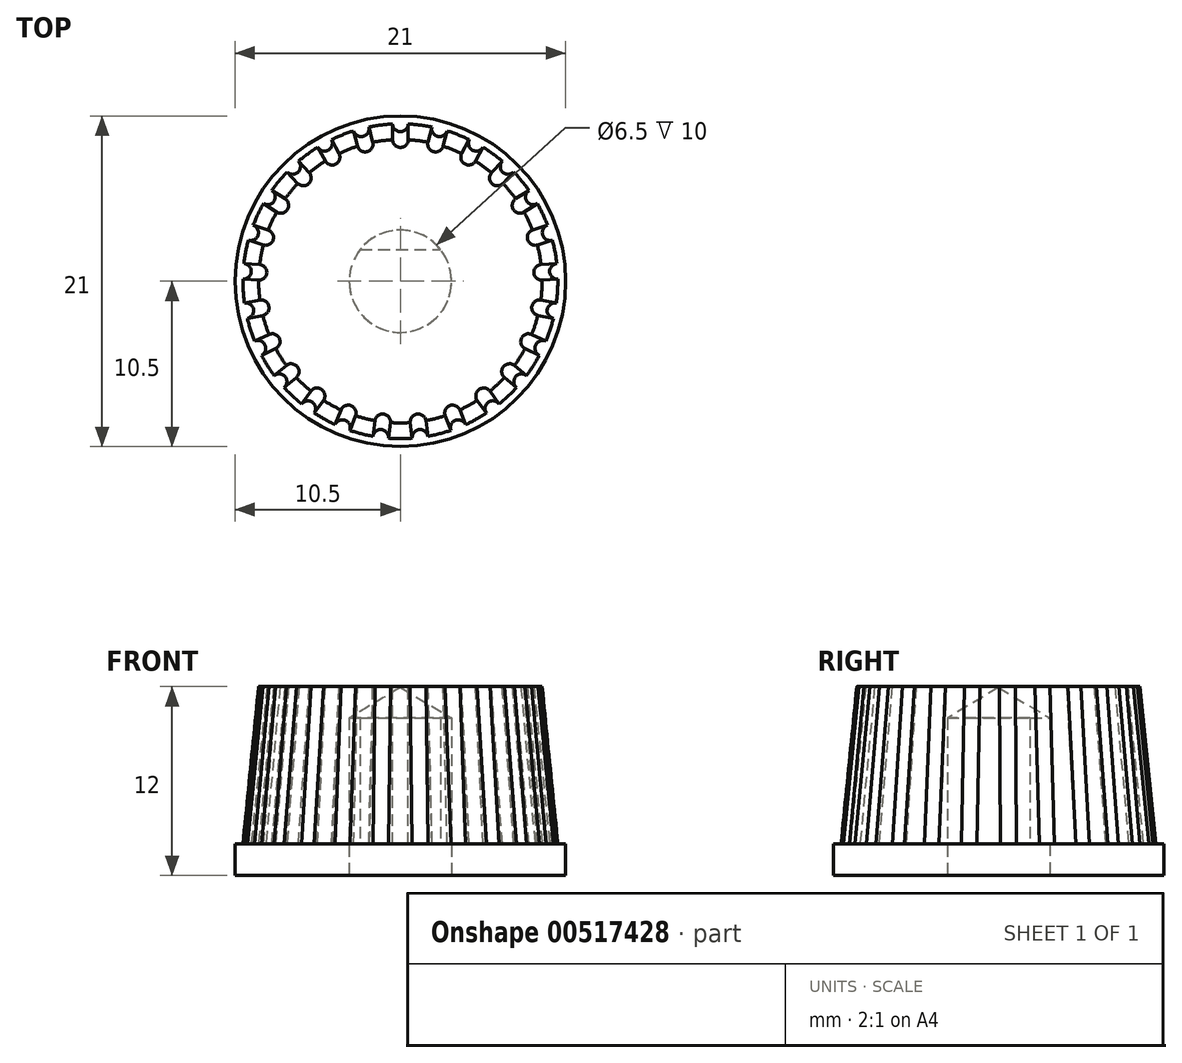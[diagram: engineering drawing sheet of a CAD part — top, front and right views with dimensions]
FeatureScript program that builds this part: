
annotation { "Feature Type Name" : "Feature", "Feature Type Description" : "" }
export const myFeature = defineFeature(function(context is Context, id is Id, definition is map)
    precondition{}
    {
        {
            var Q0;
            Q0=qCreatedBy(makeId("Top.planeOp"),FACE);
            var sketch = newSketch(context, id + "F0", { "sketchPlane" : qUnion([Q0])});
            skCircle(sketch, "E0", {"center": v(0, 0) * mm, "radius": 10 * mm});
            skArc(sketch, "E1", {"start": v(-0.5, 9.99) * mm, "mid": v(0, 9.5) * mm, "end": v(0.5, 9.99) * mm});
            skArc(sketch, "E2.1.0", {"start": v(-2.97, 9.55) * mm, "mid": v(-2.36, 9.2) * mm, "end": v(-2, 9.8) * mm});
            skArc(sketch, "E2.2.0", {"start": v(-5.25, 8.51) * mm, "mid": v(-4.58, 8.32) * mm, "end": v(-4.37, 9) * mm});
            skArc(sketch, "E2.3.0", {"start": v(-7.2, 6.94) * mm, "mid": v(-6.5, 6.93) * mm, "end": v(-6.47, 7.62) * mm});
            skArc(sketch, "E2.4.0", {"start": v(-8.7, 4.93) * mm, "mid": v(-8.02, 5.1) * mm, "end": v(-8.16, 5.77) * mm});
            skArc(sketch, "E2.5.0", {"start": v(-9.65, 2.61) * mm, "mid": v(-9.04, 2.94) * mm, "end": v(-9.34, 3.56) * mm});
            skArc(sketch, "E2.6.0", {"start": v(-10, 0.13) * mm, "mid": v(-9.48, 0.6) * mm, "end": v(-9.94, 1.13) * mm});
            skArc(sketch, "E2.7.0", {"start": v(-9.72, -2.36) * mm, "mid": v(-9.33, -1.78) * mm, "end": v(-9.9, -1.38) * mm});
            skArc(sketch, "E2.8.0", {"start": v(-8.82, -4.7) * mm, "mid": v(-8.6, -4.04) * mm, "end": v(-9.25, -3.8) * mm});
            skArc(sketch, "E2.9.0", {"start": v(-7.38, -6.75) * mm, "mid": v(-7.32, -6.06) * mm, "end": v(-8.01, -5.98) * mm});
            skArc(sketch, "E2.10.0", {"start": v(-5.47, -8.37) * mm, "mid": v(-5.58, -7.69) * mm, "end": v(-6.27, -7.79) * mm});
            skArc(sketch, "E2.11.0", {"start": v(-3.21, -9.47) * mm, "mid": v(-3.5, -8.83) * mm, "end": v(-4.14, -9.1) * mm});
            skArc(sketch, "E2.12.0", {"start": v(-0.76, -9.97) * mm, "mid": v(-1.2, -9.43) * mm, "end": v(-1.75, -9.85) * mm});
            skArc(sketch, "E2.13.0", {"start": v(1.75, -9.85) * mm, "mid": v(1.2, -9.43) * mm, "end": v(0.76, -9.97) * mm});
            skArc(sketch, "E2.14.0", {"start": v(4.14, -9.1) * mm, "mid": v(3.5, -8.83) * mm, "end": v(3.21, -9.47) * mm});
            skArc(sketch, "E2.15.0", {"start": v(6.27, -7.79) * mm, "mid": v(5.58, -7.69) * mm, "end": v(5.47, -8.37) * mm});
            skArc(sketch, "E2.16.0", {"start": v(8.01, -5.98) * mm, "mid": v(7.32, -6.06) * mm, "end": v(7.38, -6.75) * mm});
            skArc(sketch, "E2.17.0", {"start": v(9.25, -3.8) * mm, "mid": v(8.6, -4.04) * mm, "end": v(8.82, -4.7) * mm});
            skArc(sketch, "E2.18.0", {"start": v(9.9, -1.38) * mm, "mid": v(9.33, -1.78) * mm, "end": v(9.72, -2.36) * mm});
            skArc(sketch, "E2.19.0", {"start": v(9.94, 1.13) * mm, "mid": v(9.48, 0.6) * mm, "end": v(10, 0.13) * mm});
            skArc(sketch, "E2.20.0", {"start": v(9.34, 3.56) * mm, "mid": v(9.04, 2.94) * mm, "end": v(9.65, 2.61) * mm});
            skArc(sketch, "E2.21.0", {"start": v(8.16, 5.77) * mm, "mid": v(8.02, 5.1) * mm, "end": v(8.7, 4.93) * mm});
            skArc(sketch, "E2.22.0", {"start": v(6.47, 7.62) * mm, "mid": v(6.5, 6.93) * mm, "end": v(7.2, 6.94) * mm});
            skArc(sketch, "E2.23.0", {"start": v(4.37, 9) * mm, "mid": v(4.58, 8.32) * mm, "end": v(5.25, 8.51) * mm});
            skArc(sketch, "E2.24.0", {"start": v(2, 9.8) * mm, "mid": v(2.36, 9.2) * mm, "end": v(2.97, 9.55) * mm});
            skSolve(sketch);
        }
        {
            var Q0;
            Q0=qCreatedBy(makeId("Top.planeOp"),FACE);
            cPlane(context, id + "F1", {"entities" : qUnion([Q0]), "cplaneType" : CPlaneType.OFFSET, "offset" : 10 * mm, "width" : 150 * mm, "height" : 150 * mm});
        }
        {
            var Q0;
            Q0=qCreatedBy(id+"F1.planeOp",FACE);
            var sketch = newSketch(context, id + "F2", { "sketchPlane" : qUnion([Q0])});
            skCircle(sketch, "E3", {"center": v(0, 0) * mm, "radius": 9 * mm});
            skArc(sketch, "E4", {"start": v(-0.5, 8.99) * mm, "mid": v(0, 8.5) * mm, "end": v(0.5, 8.99) * mm});
            skArc(sketch, "E5.1.0", {"start": v(-2.72, 8.58) * mm, "mid": v(-2.11, 8.23) * mm, "end": v(-1.75, 8.83) * mm});
            skArc(sketch, "E5.2.0", {"start": v(-4.77, 7.63) * mm, "mid": v(-4.1, 7.45) * mm, "end": v(-3.9, 8.12) * mm});
            skArc(sketch, "E5.3.0", {"start": v(-6.52, 6.2) * mm, "mid": v(-5.82, 6.2) * mm, "end": v(-5.79, 6.9) * mm});
            skArc(sketch, "E5.4.0", {"start": v(-7.86, 4.4) * mm, "mid": v(-7.18, 4.55) * mm, "end": v(-7.32, 5.24) * mm});
            skArc(sketch, "E5.5.0", {"start": v(-8.7, 2.3) * mm, "mid": v(-8.08, 2.63) * mm, "end": v(-8.4, 3.25) * mm});
            skArc(sketch, "E5.6.0", {"start": v(-9, 0.07) * mm, "mid": v(-8.48, 0.53) * mm, "end": v(-8.94, 1.06) * mm});
            skArc(sketch, "E5.7.0", {"start": v(-8.73, -2.17) * mm, "mid": v(-8.35, -1.6) * mm, "end": v(-8.92, -1.2) * mm});
            skArc(sketch, "E5.8.0", {"start": v(-7.92, -4.28) * mm, "mid": v(-7.7, -3.62) * mm, "end": v(-8.34, -3.37) * mm});
            skArc(sketch, "E5.9.0", {"start": v(-6.6, -6.11) * mm, "mid": v(-6.55, -5.42) * mm, "end": v(-7.24, -5.34) * mm});
            skArc(sketch, "E5.10.0", {"start": v(-4.88, -7.56) * mm, "mid": v(-5, -6.88) * mm, "end": v(-5.69, -6.98) * mm});
            skArc(sketch, "E5.11.0", {"start": v(-2.84, -8.54) * mm, "mid": v(-3.13, -7.9) * mm, "end": v(-3.77, -8.17) * mm});
            skArc(sketch, "E5.12.0", {"start": v(-0.63, -8.98) * mm, "mid": v(-1.07, -8.43) * mm, "end": v(-1.62, -8.85) * mm});
            skArc(sketch, "E5.13.0", {"start": v(1.62, -8.85) * mm, "mid": v(1.07, -8.43) * mm, "end": v(0.63, -8.98) * mm});
            skArc(sketch, "E5.14.0", {"start": v(3.77, -8.17) * mm, "mid": v(3.13, -7.9) * mm, "end": v(2.84, -8.54) * mm});
            skArc(sketch, "E5.15.0", {"start": v(5.69, -6.98) * mm, "mid": v(5, -6.88) * mm, "end": v(4.88, -7.56) * mm});
            skArc(sketch, "E5.16.0", {"start": v(7.24, -5.34) * mm, "mid": v(6.55, -5.42) * mm, "end": v(6.6, -6.11) * mm});
            skArc(sketch, "E5.17.0", {"start": v(8.34, -3.37) * mm, "mid": v(7.7, -3.62) * mm, "end": v(7.92, -4.28) * mm});
            skArc(sketch, "E5.18.0", {"start": v(8.92, -1.2) * mm, "mid": v(8.35, -1.6) * mm, "end": v(8.73, -2.17) * mm});
            skArc(sketch, "E5.19.0", {"start": v(8.94, 1.06) * mm, "mid": v(8.48, 0.53) * mm, "end": v(9, 0.07) * mm});
            skArc(sketch, "E5.20.0", {"start": v(8.4, 3.25) * mm, "mid": v(8.08, 2.63) * mm, "end": v(8.7, 2.3) * mm});
            skArc(sketch, "E5.21.0", {"start": v(7.32, 5.24) * mm, "mid": v(7.18, 4.55) * mm, "end": v(7.86, 4.4) * mm});
            skArc(sketch, "E5.22.0", {"start": v(5.79, 6.9) * mm, "mid": v(5.82, 6.2) * mm, "end": v(6.52, 6.2) * mm});
            skArc(sketch, "E5.23.0", {"start": v(3.9, 8.12) * mm, "mid": v(4.1, 7.45) * mm, "end": v(4.77, 7.63) * mm});
            skArc(sketch, "E5.24.0", {"start": v(1.75, 8.83) * mm, "mid": v(2.11, 8.23) * mm, "end": v(2.72, 8.58) * mm});
            skSolve(sketch);
        }
        {
            var Q0;
            {var subQ18=sQuery(id+"F0.wireOp",EDGE,"E1");Q0=makeQuery(id+"F0.imprint","IMPRINT",FACE,{"disambiguationData":[TD([[makeQuery(id+"F0.imprint","IMPRINT",EDGE,{"derivedFrom":subQ18}),-1.0]])]});}
            var Q1;
            {var subQ18=sQuery(id+"F2.wireOp",EDGE,"E4");Q1=makeQuery(id+"F2.imprint","IMPRINT",FACE,{"disambiguationData":[TD([[makeQuery(id+"F2.imprint","IMPRINT",EDGE,{"derivedFrom":subQ18}),-1.0]])]});}
            loft(context, id + "F3", {"sheetProfilesArray" : [{ "sheetProfileEntities" : qUnion([Q0]) }, { "sheetProfileEntities" : qUnion([Q1]) }]});
        }
        {
            var Q0;
            Q0=qCreatedBy(makeId("Top.planeOp"),FACE);
            var sketch = newSketch(context, id + "F4", { "sketchPlane" : qUnion([Q0])});
            skCircle(sketch, "E6", {"center": v(0, 0) * mm, "radius": 10.5 * mm});
            skSolve(sketch);
        }
        {
            var Q0;
            Q0=makeQuery(id+"F4.imprint","IMPRINT",FACE,{"disambiguationData":[TD([[makeQuery(id+"F4.imprint","IMPRINT",EDGE,{"derivedFrom":sQuery(id+"F4.wireOp",EDGE,"E6")}),1.0]])]});
            extrude(context, id + "F5", {"entities" : qUnion([Q0]), "operationType" : NewBodyOperationType.ADD, "oppositeDirection" : true, "depth" : 2 * mm, "offsetDistance" : 25 * mm});
        }
        {
            var Q0;
            Q0=makeQuery(id+"F5.opExtrude","CAP_FACE",FACE,{"disambiguationData":[OSD([sQuery(id+"F4.wireOp",EDGE,"E6")])],"isStart":false});
            var sketch = newSketch(context, id + "F6", { "sketchPlane" : qUnion([Q0])});
            skPoint(sketch, "E7", {"position": v(0, 0) * mm});
            skSolve(sketch);
        }
        {
            var Q0;
            Q0=sQuery(id+"F6.wireOp",VERTEX,"E7");
            var Q1;
            {var subQ18=sQuery(id+"F2.wireOp",EDGE,"E4");var subQ44=sQuery(id+"F0.wireOp",EDGE,"E1");Q1=makeQuery(id+"F3.opLoft","SWEPT_BODY",BODY,{"disambiguationData":[OSD([makeQuery(id+"F0.imprint","IMPRINT",FACE,{"disambiguationData":[TD([[makeQuery(id+"F0.imprint","IMPRINT",EDGE,{"derivedFrom":subQ44}),-1.0]])]}),makeQuery(id+"F2.imprint","IMPRINT",FACE,{"disambiguationData":[TD([[makeQuery(id+"F2.imprint","IMPRINT",EDGE,{"derivedFrom":subQ18}),-1.0]])]})])]});}
            hole(context, id + "F7", {"style" : HoleStyle.SIMPLE, "endStyle" : HoleEndStyle.BLIND, "holeDiameter" : 6.5 * mm, "holeDepth" : 10 * mm, "isTappedThrough" : true, "tappedDepth" : 12 * mm, "tapClearance" : 3, "locations" : qUnion([Q0]), "scope" : qUnion([Q1])});
        }
        {
            var Q0;
            Q0=qCreatedBy(makeId("Top.planeOp"),FACE);
            var sketch = newSketch(context, id + "F8", { "sketchPlane" : qUnion([Q0])});
            skLineSegment(sketch, "E8", {"start": v(-2.56, 2) * mm, "end": v(2.56, 2) * mm});
            skArc(sketch, "E9", {"start": v(2.56, 2) * mm, "mid": v(0, 3.25) * mm, "end": v(-2.56, 2) * mm});
            skSolve(sketch);
        }
        {
            var Q0;
            Q0=makeQuery(id+"F8.imprint","IMPRINT",FACE,{"disambiguationData":[TD([[makeQuery(id+"F8.imprint","IMPRINT",EDGE,{"derivedFrom":sQuery(id+"F8.wireOp",EDGE,"E8")}),1.0]])]});
            extrude(context, id + "F9", {"entities" : qUnion([Q0]), "operationType" : NewBodyOperationType.ADD, "depth" : 8 * mm, "offsetDistance" : 25 * mm});
        }
    });
